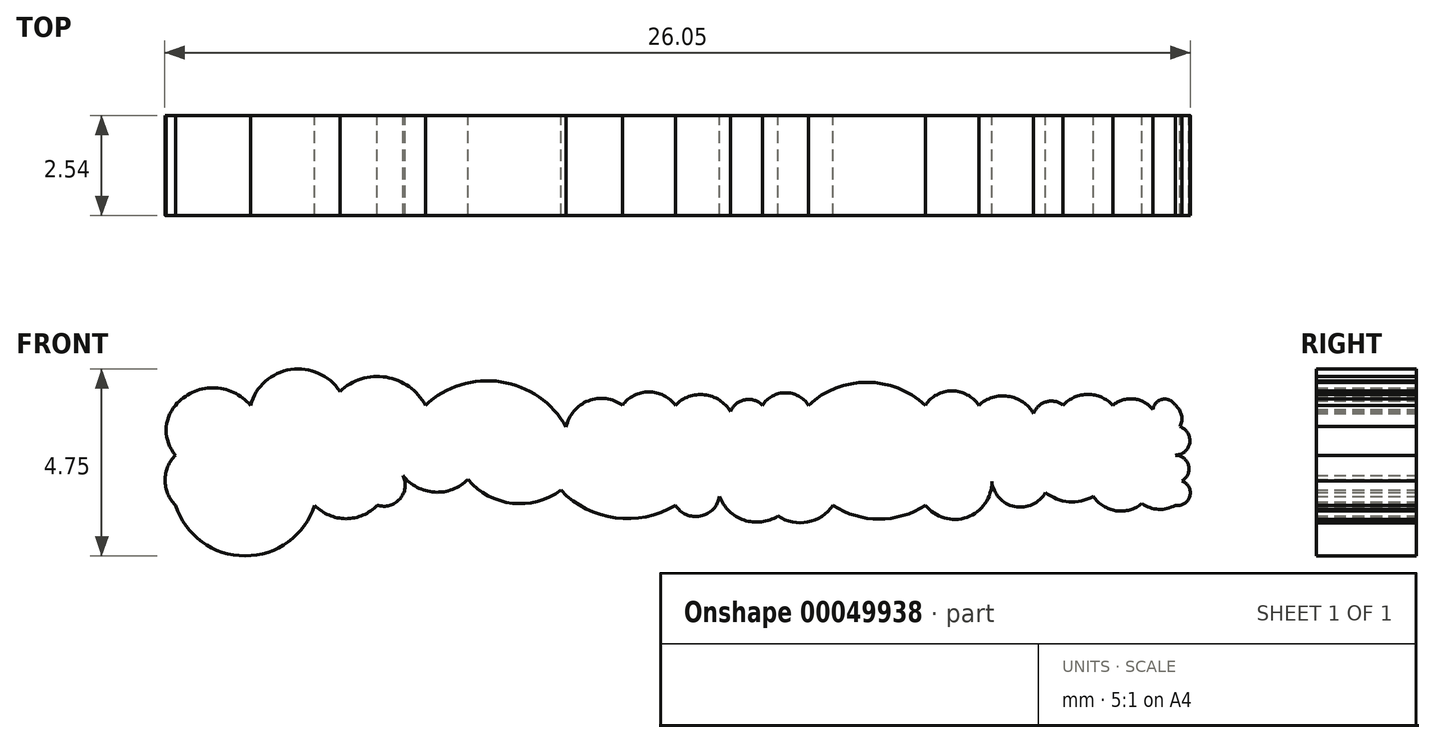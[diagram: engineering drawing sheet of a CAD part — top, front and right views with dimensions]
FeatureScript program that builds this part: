
annotation { "Feature Type Name" : "Feature", "Feature Type Description" : "" }
export const myFeature = defineFeature(function(context is Context, id is Id, definition is map)
    precondition{}
    {
        {
            var Q0;
            Q0=qCreatedBy(makeId("Front.planeOp"),FACE);
            var sketch = newSketch(context, id + "F0", { "sketchPlane" : qUnion([Q0])});
            skLineSegment(sketch, "E0", {"start": v(0, 0) * mm, "end": v(25.4, 0) * mm, "construction": true});
            skLineSegment(sketch, "E1", {"start": v(25.4, 0) * mm, "end": v(25.4, 2.54) * mm, "construction": true});
            skLineSegment(sketch, "E2", {"start": v(25.4, 2.54) * mm, "end": v(0, 2.54) * mm, "construction": true});
            skLineSegment(sketch, "E3", {"start": v(0, 2.54) * mm, "end": v(0, 0) * mm, "construction": true});
            skLineSegment(sketch, "E4", {"start": v(0, 1.27) * mm, "end": v(25.4, 1.27) * mm, "construction": true});
            skLineSegment(sketch, "E5", {"start": v(12.7, 2.54) * mm, "end": v(12.7, 0) * mm, "construction": true});
            skLineSegment(sketch, "E6", {"start": v(12.7, 0) * mm, "end": v(25.4, 2.54) * mm, "construction": true});
            skLineSegment(sketch, "E7", {"start": v(25.4, 0) * mm, "end": v(12.7, 2.54) * mm, "construction": true});
            skLineSegment(sketch, "E8", {"start": v(12.7, 2.54) * mm, "end": v(0, 0) * mm, "construction": true});
            skLineSegment(sketch, "E9", {"start": v(0, 2.54) * mm, "end": v(12.7, 0) * mm, "construction": true});
            skLineSegment(sketch, "E10", {"start": v(6.35, 1.27) * mm, "end": v(6.35, 2.54) * mm, "construction": true});
            skLineSegment(sketch, "E11", {"start": v(6.35, 2.54) * mm, "end": v(6.35, 0) * mm, "construction": true});
            skLineSegment(sketch, "E12", {"start": v(19.05, 1.27) * mm, "end": v(19.05, 2.54) * mm, "construction": true});
            skLineSegment(sketch, "E13", {"start": v(19.05, 2.54) * mm, "end": v(19.05, 0) * mm, "construction": true});
            skLineSegment(sketch, "E14", {"start": v(0, 2.54) * mm, "end": v(2.54, 2.54) * mm});
            skLineSegment(sketch, "E15", {"start": v(2.54, 2.54) * mm, "end": v(2.54, 3.68) * mm});
            skArc(sketch, "E16", {"start": v(19.05, 2.54) * mm, "mid": v(17.2, 3.1) * mm, "end": v(15.63, 1.95) * mm});
            skArc(sketch, "E17", {"start": v(9.93, 1.99) * mm, "mid": v(8.27, 3.13) * mm, "end": v(6.35, 2.54) * mm});
            skArc(sketch, "E18", {"start": v(11.35, 2.54) * mm, "mid": v(10.49, 2.65) * mm, "end": v(9.93, 1.99) * mm});
            skArc(sketch, "E19", {"start": v(12.7, 2.54) * mm, "mid": v(12.03, 2.88) * mm, "end": v(11.35, 2.54) * mm});
            skArc(sketch, "E20", {"start": v(0, 1.27) * mm, "mid": v(-0.27, 0.63) * mm, "end": v(0, 0) * mm});
            skArc(sketch, "E21", {"start": v(0, 0) * mm, "mid": v(1.77, -1.29) * mm, "end": v(3.54, 0) * mm});
            skArc(sketch, "E22", {"start": v(3.54, 0) * mm, "mid": v(4.33, -0.34) * mm, "end": v(5.13, 0) * mm});
            skArc(sketch, "E23", {"start": v(5.13, 0) * mm, "mid": v(5.83, 0.44) * mm, "end": v(5.28, 1.06) * mm});
            skArc(sketch, "E24", {"start": v(5.78, 0.75) * mm, "mid": v(6.8, 0.34) * mm, "end": v(7.67, 1) * mm});
            skArc(sketch, "E25", {"start": v(7.43, 0.65) * mm, "mid": v(8.68, 0.04) * mm, "end": v(9.98, 0.54) * mm});
            skArc(sketch, "E26", {"start": v(9.8, 0.38) * mm, "mid": v(11.18, -0.32) * mm, "end": v(12.7, 0) * mm});
            skArc(sketch, "E27", {"start": v(12.7, 0) * mm, "mid": v(13.34, -0.28) * mm, "end": v(13.82, 0.22) * mm});
            skArc(sketch, "E28", {"start": v(13.82, 0.22) * mm, "mid": v(14.44, -0.38) * mm, "end": v(15.3, -0.28) * mm});
            skPoint(sketch, "E28.endSnap0", {"position": v(13.34, -0.28) * mm});
            skArc(sketch, "E29", {"start": v(15.3, -0.28) * mm, "mid": v(16.46, -0.26) * mm, "end": v(16.84, 0.83) * mm});
            skArc(sketch, "E30", {"start": v(16.7, 0) * mm, "mid": v(17.88, -0.35) * mm, "end": v(19.05, 0) * mm});
            skArc(sketch, "E31", {"start": v(19.05, 0) * mm, "mid": v(20.27, -0.23) * mm, "end": v(20.67, 0.95) * mm});
            skArc(sketch, "E32", {"start": v(20.74, 0.6) * mm, "mid": v(21.49, -0.05) * mm, "end": v(22.2, 0.64) * mm});
            skArc(sketch, "E33", {"start": v(22.1, 0.32) * mm, "mid": v(22.83, 0.09) * mm, "end": v(23.53, 0.37) * mm});
            skArc(sketch, "E34", {"start": v(23.32, 0.22) * mm, "mid": v(23.97, -0.15) * mm, "end": v(24.66, 0.15) * mm});
            skArc(sketch, "E35", {"start": v(24.56, 0.04) * mm, "mid": v(24.97, -0.1) * mm, "end": v(25.4, 0) * mm});
            skArc(sketch, "E36", {"start": v(0, 2.54) * mm, "mid": v(-0.24, 1.9) * mm, "end": v(0, 1.27) * mm});
            skArc(sketch, "E37", {"start": v(1.9, 2.54) * mm, "mid": v(0.95, 2.98) * mm, "end": v(0, 2.54) * mm});
            skArc(sketch, "E38", {"start": v(4.33, 2.54) * mm, "mid": v(3.12, 3.46) * mm, "end": v(1.9, 2.54) * mm});
            skArc(sketch, "E39", {"start": v(6.35, 2.54) * mm, "mid": v(5.35, 3.25) * mm, "end": v(4.18, 2.89) * mm});
            skArc(sketch, "E40", {"start": v(14.17, 2.25) * mm, "mid": v(13.51, 2.8) * mm, "end": v(12.7, 2.54) * mm});
            skArc(sketch, "E41", {"start": v(14.92, 2.54) * mm, "mid": v(14.46, 2.68) * mm, "end": v(14.1, 2.38) * mm});
            skArc(sketch, "E42", {"start": v(16.08, 2.54) * mm, "mid": v(15.5, 2.86) * mm, "end": v(14.92, 2.54) * mm});
            skArc(sketch, "E43", {"start": v(20.4, 2.54) * mm, "mid": v(19.73, 2.9) * mm, "end": v(19.05, 2.54) * mm});
            skArc(sketch, "E44", {"start": v(21.93, 1.85) * mm, "mid": v(21.4, 2.7) * mm, "end": v(20.4, 2.54) * mm});
            skArc(sketch, "E45", {"start": v(22.55, 2.54) * mm, "mid": v(22.12, 2.63) * mm, "end": v(21.8, 2.33) * mm});
            skArc(sketch, "E46", {"start": v(23.81, 2.54) * mm, "mid": v(23.18, 2.82) * mm, "end": v(22.55, 2.54) * mm});
            skArc(sketch, "E47", {"start": v(24.83, 2.43) * mm, "mid": v(24.35, 2.7) * mm, "end": v(23.81, 2.54) * mm});
            skArc(sketch, "E48", {"start": v(25.4, 2.54) * mm, "mid": v(25.07, 2.69) * mm, "end": v(24.83, 2.43) * mm});
            skArc(sketch, "E49", {"start": v(25.4, 1.85) * mm, "mid": v(25.57, 2.2) * mm, "end": v(25.4, 2.54) * mm});
            skArc(sketch, "E50", {"start": v(25.4, 1.27) * mm, "mid": v(25.77, 1.58) * mm, "end": v(25.52, 2) * mm});
            skArc(sketch, "E51", {"start": v(25.4, 0) * mm, "mid": v(25.78, 0.31) * mm, "end": v(25.4, 0.63) * mm});
            skArc(sketch, "E52", {"start": v(25.57, 0.62) * mm, "mid": v(25.74, 1) * mm, "end": v(25.4, 1.27) * mm});
            skSolve(sketch);
        }
        {
            var Q0;
            Q0 = qSketchRegion(id + "F0", true);
            extrude(context, id + "F1", {"entities" : qUnion([Q0]), "depth" : 2.54 * mm});
        }
    });
